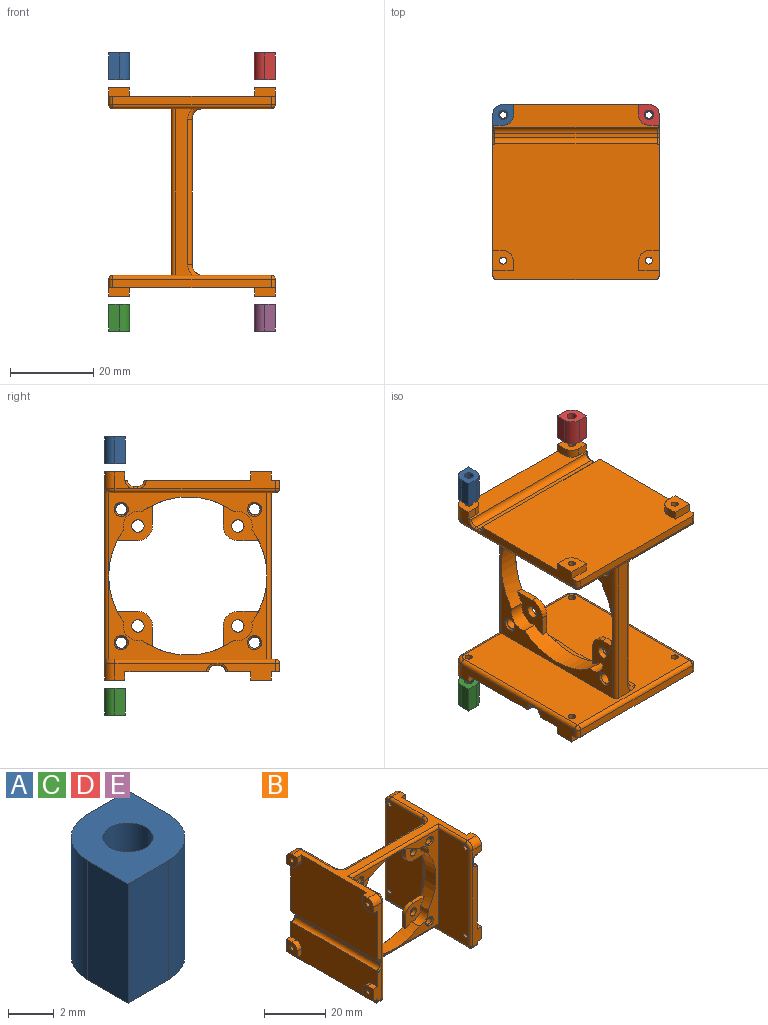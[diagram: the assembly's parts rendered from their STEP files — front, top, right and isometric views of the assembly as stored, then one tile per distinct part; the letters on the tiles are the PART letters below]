
ASSEMBLY  parts=5 mates=4
PART A: 9 faces, bbox 5x5x6.4 mm
  f0: plane 6.4x2.5mm, normal (1,0,0), area 16mm2, adj f1,f5,f6,f7
  f1: plane 6.4x2.5mm, normal (0,1,0), area 16mm2, adj f0,f2,f6,f7
  f2: cylinder r=2.5mm len=6.4mm, axis (0,0,-1), area 25.1mm2, adj f1,f3,f6,f7
  f3: plane 6.4x2.5mm, normal (-1,0,0), area 16mm2, adj f2,f4,f6,f7
  f4: plane 6.4x2.5mm, normal (0,-1,0), area 16mm2, adj f3,f5,f6,f7
  f5: cylinder r=2.5mm len=6.4mm, axis (0,0,-1), area 25.1mm2, adj f0,f4,f6,f7
  f6: plane 5x5mm, normal (0,0,1), area 18.5mm2, adj f0,f1,f2,f3,f4,f5,f8
  f7: plane 5x5mm, normal (0,0,-1), area 18.5mm2, adj f0,f1,f2,f3,f4,f5,f8
  f8: cylinder r=1.1mm len=6.4mm, axis (0,0,-1), area 44.2mm2, adj f6,f7
PART B: 162 faces, bbox 50.3x40.7x42.5 mm
  f0: plane 13.5x4mm, normal (0,-1,0), area 33.7mm2, adj f8,f13,f70,f73,f133,f137,f161
  f1: plane 13.5x4mm, normal (0,1,0), area 33.7mm2, adj f9,f13,f68,f69,f126,f127,f158
  f2: plane 33x4mm, normal (0,-1,0), area 72.7mm2, adj f11,f19,f85,f86,f128,f134,f155
  f3: plane 33x4mm, normal (0,1,0), area 72.7mm2, adj f10,f19,f87,f90,f122,f123,f152
  f4: plane 38x20mm, normal (0,-1,0), area 162.1mm2, adj f17,f22,f23,f29,f46,f48,f51,f57
  f5: plane 17.5x11.6mm, normal (0,1,0), area 84.9mm2, adj f23,f24,f36,f37,f38,f52,f60,f110
  f6: plane 17.5x11.6mm, normal (0,1,0), area 84.9mm2, adj f22,f29,f30,f31,f32,f50,f58,f115
  f7: plane 17.5x11.6mm, normal (0,1,0), area 84.9mm2, adj f24,f29,f33,f34,f35,f54,f61,f112
  f8: plane 4.9x2mm, normal (0,0,-1), area 9.8mm2, adj f0,f13,f72,f73
  f9: plane 4.9x2mm, normal (0,0,-1), area 9.8mm2, adj f1,f13,f66,f69
  f10: plane 4.9x2mm, normal (0,0,-1), area 9.8mm2, adj f3,f19,f89,f90
  f11: plane 4.9x2mm, normal (0,0,-1), area 9.8mm2, adj f2,f19,f83,f86
  f12: plane 40x5.5mm, normal (1,0,0), area 174.3mm2, adj f15,f18,f26,f79,f80,f81,f92,f93
  f13: plane 40x13mm, normal (-1,0,0), area 473.9mm2, adj f0,f1,f8,f9,f66,f67,f68,f70
  f14: plane 24x4mm, normal (0,1,0), area 49.7mm2, adj f20,f63,f65,f104,f126,f156
  f15: plane 4.5x4mm, normal (0,1,0), area 10.7mm2, adj f12,f91,f94,f95,f123,f150
  f16: plane 40.29x38.29mm, normal (-1,0,0), area 1222.4mm2, adj f21,f28,f96,f97,f98,f99,f110,f111
  f17: plane 40.29x38.29mm, normal (1,0,0), area 1222.4mm2, adj f4,f28,f100,f101,f102,f103,f113,f114
  f18: plane 50x35mm, normal (0,0,1), area 290.5mm2, adj f12,f20,f62,f65,f74,f77,f78,f81
  f19: plane 40x32.5mm, normal (1,0,0), area 1253.9mm2, adj f2,f3,f10,f11,f83,f84,f85,f87
  f20: plane 40x25mm, normal (-1,0,0), area 954.3mm2, adj f14,f18,f25,f62,f63,f64,f74,f75
  f21: plane 38x20mm, normal (0,-1,0), area 162.1mm2, adj f16,f23,f24,f29,f42,f44,f53,f55
  f22: cylinder r=19mm len=22.28mm, axis (0,-1,0), area 109.8mm2, adj f4,f6,f27,f30,f41,f46,f47,f48
  f23: cylinder r=19mm len=22.28mm, axis (0,-1,0), area 109.8mm2, adj f4,f5,f21,f27,f38,f39,f44,f45
  f24: cylinder r=19mm len=22.28mm, axis (0,-1,0), area 109.8mm2, adj f5,f7,f21,f35,f36,f42,f43,f44
  f25: plane 24x4mm, normal (0,-1,0), area 49.7mm2, adj f20,f76,f77,f105,f137,f159
  f26: plane 4.5x4mm, normal (0,-1,0), area 10.7mm2, adj f12,f78,f79,f82,f134,f153
  f27: plane 17.5x11.6mm, normal (0,1,0), area 84.9mm2, adj f22,f23,f39,f40,f41,f56,f59,f113
  f28: plane 40x4.05mm, normal (0,0,-1), area 121.6mm2, adj f16,f17,f142,f143,f144,f145
  f29: cylinder r=19mm len=22.28mm, axis (0,-1,0), area 109.8mm2, adj f4,f6,f7,f21,f32,f33,f42,f43
  f30: plane 4.99x1.5mm, normal (0,0,-1), area 7.5mm2, adj f6,f22,f31,f49
  f31: cylinder r=3.5mm len=3.5mm, axis (0,-1,0), area 8.2mm2, adj f6,f30,f32,f49
  f32: plane 4.99x1.5mm, normal (1,0,0), area 7.5mm2, adj f6,f29,f31,f49
  f33: plane 4.99x1.5mm, normal (-1,0,0), area 7.5mm2, adj f7,f29,f34,f43
  f34: cylinder r=3.5mm len=3.5mm, axis (0,-1,0), area 8.2mm2, adj f7,f33,f35,f43
  f35: plane 4.99x1.5mm, normal (0,0,-1), area 7.5mm2, adj f7,f24,f34,f43
  f36: plane 4.99x1.5mm, normal (0,0,1), area 7.5mm2, adj f5,f24,f37,f45
  f37: cylinder r=3.5mm len=3.5mm, axis (0,-1,0), area 8.2mm2, adj f5,f36,f38,f45
  f38: plane 4.99x1.5mm, normal (-1,0,0), area 7.5mm2, adj f5,f23,f37,f45
  f39: plane 4.99x1.5mm, normal (1,0,0), area 7.5mm2, adj f23,f27,f40,f47
  f40: cylinder r=3.5mm len=3.5mm, axis (0,-1,0), area 8.2mm2, adj f27,f39,f41,f47
  f41: plane 4.99x1.5mm, normal (0,0,1), area 7.5mm2, adj f22,f27,f40,f47
  f42: cylinder r=3.5mm len=4.36mm, axis (0,-1,0), area 25.3mm2, adj f21,f24,f29,f43
  f43: plane 8.49x8.49mm, normal (0,-1,0), area 40.5mm2, adj f24,f29,f33,f34,f35,f42,f61
  f44: cylinder r=3.5mm len=4.36mm, axis (0,-1,0), area 25.3mm2, adj f21,f23,f24,f45
  f45: plane 8.49x8.49mm, normal (0,-1,0), area 40.5mm2, adj f23,f24,f36,f37,f38,f44,f60
  f46: cylinder r=3.5mm len=4.36mm, axis (0,-1,0), area 25.3mm2, adj f4,f22,f23,f47
  f47: plane 8.49x8.49mm, normal (0,-1,0), area 40.5mm2, adj f22,f23,f39,f40,f41,f46,f59
  f48: cylinder r=3.5mm len=4.36mm, axis (0,-1,0), area 25.3mm2, adj f4,f22,f29,f49
  f49: plane 8.49x8.49mm, normal (0,-1,0), area 40.5mm2, adj f22,f29,f30,f31,f32,f48,f58
  f50: cylinder r=1.35mm len=4.58mm, axis (0,-1,0), area 38.9mm2, adj f6,f51
  f51: cone r=1.35mm half-angle=40deg, axis (0,-1,0), area 5.2mm2, adj f4,f50
  f52: cylinder r=1.35mm len=4.58mm, axis (0,-1,0), area 38.9mm2, adj f5,f53
  f53: cone r=1.35mm half-angle=40deg, axis (0,-1,0), area 5.2mm2, adj f21,f52
  f54: cylinder r=1.35mm len=4.58mm, axis (0,-1,0), area 38.9mm2, adj f7,f55
  f55: cone r=1.35mm half-angle=40deg, axis (0,-1,0), area 5.2mm2, adj f21,f54
  f56: cylinder r=1.35mm len=4.58mm, axis (0,-1,0), area 38.9mm2, adj f27,f57
  f57: cone r=1.35mm half-angle=40deg, axis (0,-1,0), area 5.2mm2, adj f4,f56
  f58: cylinder r=1.5mm len=3mm, axis (0,-1,0), area 14.1mm2, adj f6,f49
  f59: cylinder r=1.5mm len=3mm, axis (0,-1,0), area 14.1mm2, adj f27,f47
  f60: cylinder r=1.5mm len=3mm, axis (0,-1,0), area 14.1mm2, adj f5,f45
  f61: cylinder r=1.5mm len=3mm, axis (0,-1,0), area 14.1mm2, adj f7,f43
  f62: plane 2.5x2mm, normal (0,-1,0), area 5mm2, adj f18,f20,f64,f65
  f63: plane 2.5x2mm, normal (0,0,-1), area 5mm2, adj f14,f20,f64,f65
  f64: cylinder r=2.4mm len=2.4mm, axis (1,0,0), area 7.5mm2, adj f20,f62,f63,f65
  f65: plane 4.9x4.9mm, normal (-1,0,0), area 19.2mm2, adj f14,f18,f62,f63,f64,f103,f104
  f66: plane 2.5x2mm, normal (0,-1,0), area 5mm2, adj f9,f13,f67,f69
  f67: cylinder r=2.4mm len=2.4mm, axis (1,0,0), area 7.5mm2, adj f13,f66,f68,f69
  f68: plane 2.5x2mm, normal (0,0,1), area 5mm2, adj f1,f13,f67,f69
  f69: plane 4.9x4.9mm, normal (-1,0,0), area 20.5mm2, adj f1,f9,f66,f67,f68,f102
  f70: plane 2.5x2mm, normal (0,0,1), area 5mm2, adj f0,f13,f71,f73
  f71: cylinder r=2.4mm len=2.4mm, axis (1,0,0), area 7.5mm2, adj f13,f70,f72,f73
  f72: plane 2.5x2mm, normal (0,1,0), area 5mm2, adj f8,f13,f71,f73
  f73: plane 4.9x4.9mm, normal (-1,0,0), area 20.5mm2, adj f0,f8,f70,f71,f72,f101
  f74: plane 2.5x2mm, normal (0,1,0), area 5mm2, adj f18,f20,f75,f77
  f75: cylinder r=2.4mm len=2.4mm, axis (1,0,0), area 7.5mm2, adj f20,f74,f76,f77
  f76: plane 2.5x2mm, normal (0,0,-1), area 5mm2, adj f20,f25,f75,f77
  f77: plane 4.9x4.9mm, normal (-1,0,0), area 19.2mm2, adj f18,f25,f74,f75,f76,f100,f105
  f78: cylinder r=2.5mm len=4mm, axis (-1,0,0), area 15.7mm2, adj f18,f26,f82,f136
  f79: plane 2.5x2mm, normal (0,0,-1), area 5mm2, adj f12,f26,f80,f82
  f80: cylinder r=2.4mm len=2.4mm, axis (-1,0,0), area 7.5mm2, adj f12,f79,f81,f82
  f81: plane 2.5x2mm, normal (0,1,0), area 5mm2, adj f12,f18,f80,f82
  f82: plane 4.9x4.9mm, normal (1,0,0), area 19.2mm2, adj f18,f26,f78,f79,f80,f81,f99
  f83: plane 2.5x2mm, normal (0,1,0), area 5mm2, adj f11,f19,f84,f86
  f84: cylinder r=2.4mm len=2.4mm, axis (-1,0,0), area 7.5mm2, adj f19,f83,f85,f86
  f85: plane 2.5x2mm, normal (0,0,1), area 5mm2, adj f2,f19,f84,f86
  f86: plane 4.9x4.9mm, normal (1,0,0), area 20.5mm2, adj f2,f11,f83,f84,f85,f98
  f87: plane 2.5x2mm, normal (0,0,1), area 5mm2, adj f3,f19,f88,f90
  f88: cylinder r=2.4mm len=2.4mm, axis (-1,0,0), area 7.5mm2, adj f19,f87,f89,f90
  f89: plane 2.5x2mm, normal (0,-1,0), area 5mm2, adj f10,f19,f88,f90
  f90: plane 4.9x4.9mm, normal (1,0,0), area 20.5mm2, adj f3,f10,f87,f88,f89,f97
  f91: cylinder r=2.5mm len=4mm, axis (-1,0,0), area 15.7mm2, adj f15,f18,f95,f120
  f92: plane 2.5x2mm, normal (0,-1,0), area 5mm2, adj f12,f18,f93,f95
  f93: cylinder r=2.4mm len=2.4mm, axis (-1,0,0), area 7.5mm2, adj f12,f92,f94,f95
  f94: plane 2.5x2mm, normal (0,0,-1), area 5mm2, adj f12,f15,f93,f95
  f95: plane 4.9x4.9mm, normal (1,0,0), area 19.2mm2, adj f15,f18,f91,f92,f93,f94,f96
  f96: cylinder r=0.85mm len=5mm, axis (-1,0,0), area 26.7mm2, adj f16,f95
  f97: cylinder r=0.85mm len=5mm, axis (-1,0,0), area 26.7mm2, adj f16,f90
  f98: cylinder r=0.85mm len=5mm, axis (-1,0,0), area 26.7mm2, adj f16,f86
  f99: cylinder r=0.85mm len=5mm, axis (-1,0,0), area 26.7mm2, adj f16,f82
  f100: cylinder r=0.85mm len=5mm, axis (-1,0,0), area 26.7mm2, adj f17,f77
  f101: cylinder r=0.85mm len=5mm, axis (-1,0,0), area 26.7mm2, adj f17,f73
  f102: cylinder r=0.85mm len=5mm, axis (-1,0,0), area 26.7mm2, adj f17,f69
  f103: cylinder r=0.85mm len=5mm, axis (-1,0,0), area 26.7mm2, adj f17,f65
  f104: cylinder r=2.5mm len=4mm, axis (-1,0,0), area 15.7mm2, adj f14,f18,f65,f124
  f105: cylinder r=2.5mm len=4mm, axis (-1,0,0), area 15.7mm2, adj f18,f25,f77,f139
  f106: plane 39x1mm, normal (1,0,0), area 39mm2, adj f148,f149,f151,f154
  f107: plane 39x1mm, normal (-1,0,0), area 39mm2, adj f146,f147,f157,f160
  f108: plane 38x2mm, normal (0,0,-1), area 76mm2, adj f19,f122,f128,f129
  f109: plane 38x2mm, normal (0,0,-1), area 76mm2, adj f13,f127,f132,f133
  f110: cylinder r=2.5mm len=11.6mm, axis (0,0,1), area 45.6mm2, adj f5,f16,f111,f144
  f111: bspline ~14.8x2.5mm, area 42.6mm2, adj f16,f24,f110,f112
  f112: cylinder r=2.5mm len=11.6mm, axis (0,0,1), area 45.6mm2, adj f7,f16,f111,f116
  f113: cylinder r=2.5mm len=11.6mm, axis (0,0,1), area 45.6mm2, adj f17,f27,f114,f142
  f114: bspline ~16.32x2.95mm, area 42.6mm2, adj f17,f22,f113,f115
  f115: cylinder r=2.5mm len=11.6mm, axis (0,0,1), area 45.6mm2, adj f6,f17,f114,f119
  f116: torus R=3.5mm, axis (0,0,1), area 7.1mm2, adj f18,f112,f117,f118
  f117: cylinder r=1mm len=35mm, axis (1,0,0), area 55mm2, adj f6,f7,f18,f116,f119
  f118: cylinder r=1mm len=15mm, axis (0,1,0), area 23.6mm2, adj f16,f18,f116,f120
  f119: torus R=3.5mm, axis (0,0,1), area 7.1mm2, adj f18,f115,f117,f121
  f120: torus R=1.5mm, axis (1,0,0), area 5.3mm2, adj f16,f91,f118,f123
  f121: cylinder r=1mm len=15mm, axis (0,-1,0), area 23.6mm2, adj f17,f18,f119,f124
  f122: cylinder r=1mm len=2mm, axis (1,0,0), area 3.1mm2, adj f3,f19,f108,f125
  f123: cylinder r=1mm len=38.5mm, axis (0,0,-1), area 60.5mm2, adj f3,f15,f16,f120,f125,f151
  f124: torus R=1.5mm, axis (-1,0,0), area 5.3mm2, adj f17,f104,f121,f126
  f125: sphere r=1mm, area 1.6mm2, adj f122,f123,f129
  f126: cylinder r=1mm len=38.5mm, axis (0,0,-1), area 60.5mm2, adj f1,f14,f17,f124,f130,f157
  f127: cylinder r=1mm len=2mm, axis (1,0,0), area 3.1mm2, adj f1,f13,f109,f130
  f128: cylinder r=1mm len=2mm, axis (-1,0,0), area 3.1mm2, adj f2,f19,f108,f131
  f129: cylinder r=1mm len=38mm, axis (0,1,0), area 59.7mm2, adj f16,f108,f125,f131
  f130: sphere r=1mm, area 1.6mm2, adj f126,f127,f132
  f131: sphere r=1mm, area 1.6mm2, adj f128,f129,f134
  f132: cylinder r=1mm len=38mm, axis (0,-1,0), area 59.7mm2, adj f17,f109,f130,f135
  f133: cylinder r=1mm len=2mm, axis (-1,0,0), area 3.1mm2, adj f0,f13,f109,f135
  f134: cylinder r=1mm len=38.5mm, axis (0,0,-1), area 60.5mm2, adj f2,f16,f26,f131,f136,f154
  f135: sphere r=1mm, area 1.6mm2, adj f132,f133,f137
  f136: torus R=1.5mm, axis (1,0,0), area 5.3mm2, adj f16,f78,f134,f138
  f137: cylinder r=1mm len=38.5mm, axis (0,0,-1), area 60.5mm2, adj f0,f17,f25,f135,f139,f160
  f138: cylinder r=1mm len=13.5mm, axis (0,1,0), area 20.4mm2, adj f16,f18,f136,f140
  f139: torus R=1.5mm, axis (-1,0,0), area 5.3mm2, adj f17,f105,f137,f141
  f140: cylinder r=1mm len=42mm, axis (-1,0,0), area 64.4mm2, adj f4,f18,f21,f138,f141
  f141: cylinder r=1mm len=13.5mm, axis (0,-1,0), area 20.4mm2, adj f17,f18,f139,f140
  f142: torus R=3.5mm, axis (0,0,1), area 5.2mm2, adj f17,f28,f113,f143
  f143: cylinder r=1mm len=35mm, axis (-1,0,0), area 55mm2, adj f5,f27,f28,f142,f144
  f144: torus R=3.5mm, axis (0,0,1), area 5.2mm2, adj f16,f28,f110,f143
  f145: cylinder r=1mm len=40mm, axis (1,0,0), area 62.8mm2, adj f4,f16,f17,f21,f28
  f146: cylinder r=1.5mm len=39mm, axis (0,1,0), area 91.9mm2, adj f13,f107,f158,f161
  f147: cylinder r=1.5mm len=39mm, axis (0,1,0), area 91.9mm2, adj f20,f107,f156,f159
  f148: cylinder r=1.5mm len=39mm, axis (0,1,0), area 91.9mm2, adj f12,f106,f150,f153
  f149: cylinder r=1.5mm len=39mm, axis (0,1,0), area 91.9mm2, adj f19,f106,f152,f155
  f150: torus R=2mm, axis (0,-1,0), area 2.1mm2, adj f12,f15,f148,f151
  f151: cylinder r=0.5mm len=1mm, axis (0,0,-1), area 0.8mm2, adj f106,f123,f150,f152
  f152: torus R=2mm, axis (0,-1,0), area 2.1mm2, adj f3,f19,f149,f151
  f153: torus R=2mm, axis (0,1,0), area 2.1mm2, adj f12,f26,f148,f154
  f154: cylinder r=0.5mm len=1mm, axis (0,0,-1), area 0.8mm2, adj f106,f134,f153,f155
  f155: torus R=2mm, axis (0,1,0), area 2.1mm2, adj f2,f19,f149,f154
  f156: torus R=2mm, axis (0,-1,0), area 2.1mm2, adj f14,f20,f147,f157
  f157: cylinder r=0.5mm len=1mm, axis (0,0,1), area 0.8mm2, adj f107,f126,f156,f158
  f158: torus R=2mm, axis (0,-1,0), area 2.1mm2, adj f1,f13,f146,f157
  f159: torus R=2mm, axis (0,1,0), area 2.1mm2, adj f20,f25,f147,f160
  f160: cylinder r=0.5mm len=1mm, axis (0,0,1), area 0.8mm2, adj f107,f137,f159,f161
  f161: torus R=2mm, axis (0,1,0), area 2.1mm2, adj f0,f13,f146,f160
PART C: same geometry as A
PART D: same geometry as A
PART E: same geometry as A
PLACE A rot(axis=(0,0,1),180deg) t=(22.31,74.51,78.31)mm
PLACE B rot(axis=(-0.58,-0.58,-0.58),120deg) t=(-10.81,-24.81,79.79)mm
PLACE C t=(-20.17,-49.12,17.91)mm
PLACE D rot(axis=(1,0,0),180deg) t=(14.83,74.51,84.71)mm
PLACE E rot(axis=(1,0,0),180deg) t=(14.83,74.51,24.31)mm
MATE fastened B.f136 <-> C.f2  axis (0,0,-1) through (1.07,12.69,24.31)mm
MATE fastened B.f120 <-> E.f2  axis (0,0,-1) through (36.07,12.69,24.31)mm
MATE fastened A.f2 <-> B.f75  axis (0,0,-1) through (1.07,12.69,78.31)mm
MATE fastened B.f64 <-> D.f2  axis (0,0,1) through (36.07,12.69,78.31)mm
